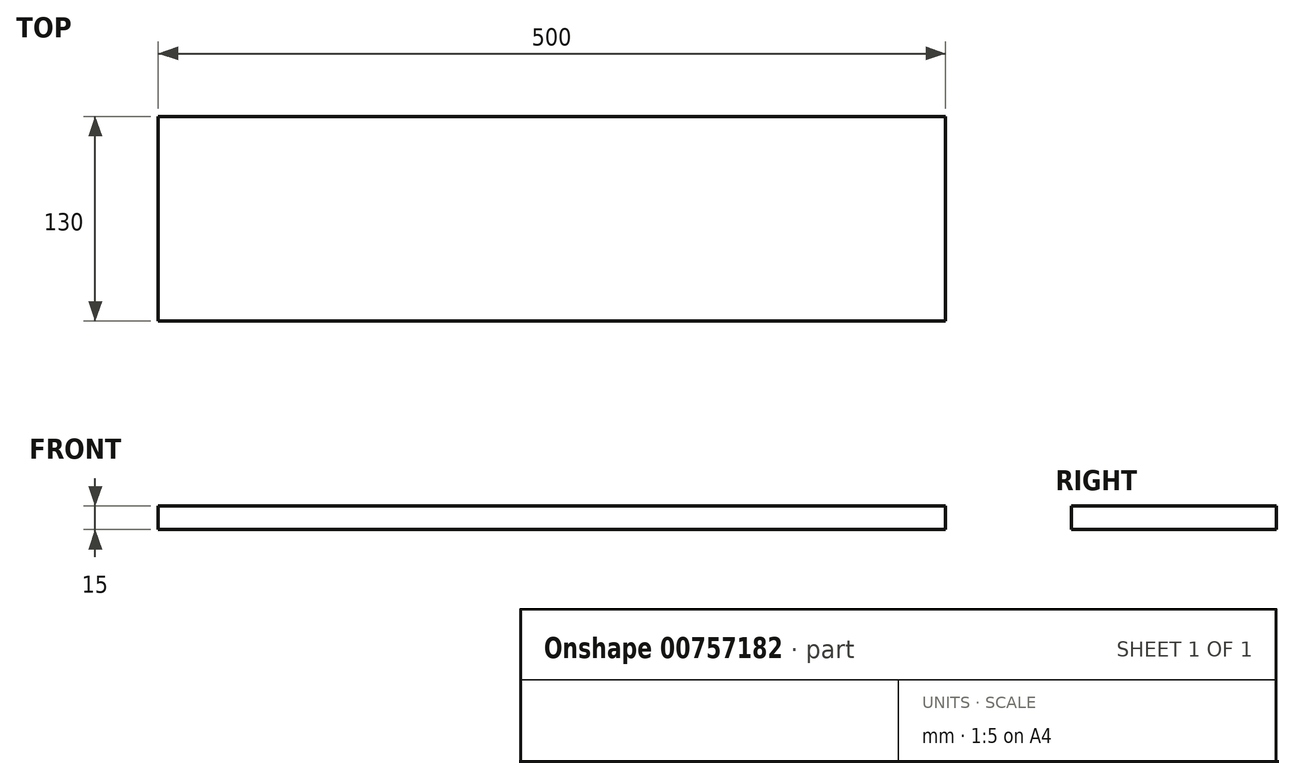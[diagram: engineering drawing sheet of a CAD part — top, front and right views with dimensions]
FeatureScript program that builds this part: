
annotation { "Feature Type Name" : "Feature", "Feature Type Description" : "" }
export const myFeature = defineFeature(function(context is Context, id is Id, definition is map)
    precondition{}
    {
        {
            var Q0;
            Q0=qCreatedBy(makeId("Right.planeOp"),FACE);
            var sketch = newSketch(context, id + "F0", { "sketchPlane" : qUnion([Q0])});
            skLineSegment(sketch, "E0.bottom", {"start": v(-65, 0) * mm, "end": v(65, 0) * mm});
            skLineSegment(sketch, "E0.top", {"start": v(-65, 15) * mm, "end": v(65, 15) * mm});
            skLineSegment(sketch, "E0.left", {"start": v(-65, 15) * mm, "end": v(-65, 0) * mm});
            skLineSegment(sketch, "E0.right", {"start": v(65, 15) * mm, "end": v(65, 0) * mm});
            skSolve(sketch);
        }
        {
            var Q0;
            Q0=makeQuery(id+"F0.imprint","IMPRINT",FACE,{"disambiguationData":[TD([[makeQuery(id+"F0.imprint","IMPRINT",EDGE,{"derivedFrom":sQuery(id+"F0.wireOp",EDGE,"E0.bottom")}),1.0]])]});
            extrude(context, id + "F1", {"entities" : qUnion([Q0]), "oppositeDirection" : true, "depth" : 250 * mm, "offsetDistance" : 25 * mm, "hasSecondDirection" : true, "secondDirectionOppositeDirection" : false, "secondDirectionDepth" : 250 * mm});
        }
    });
